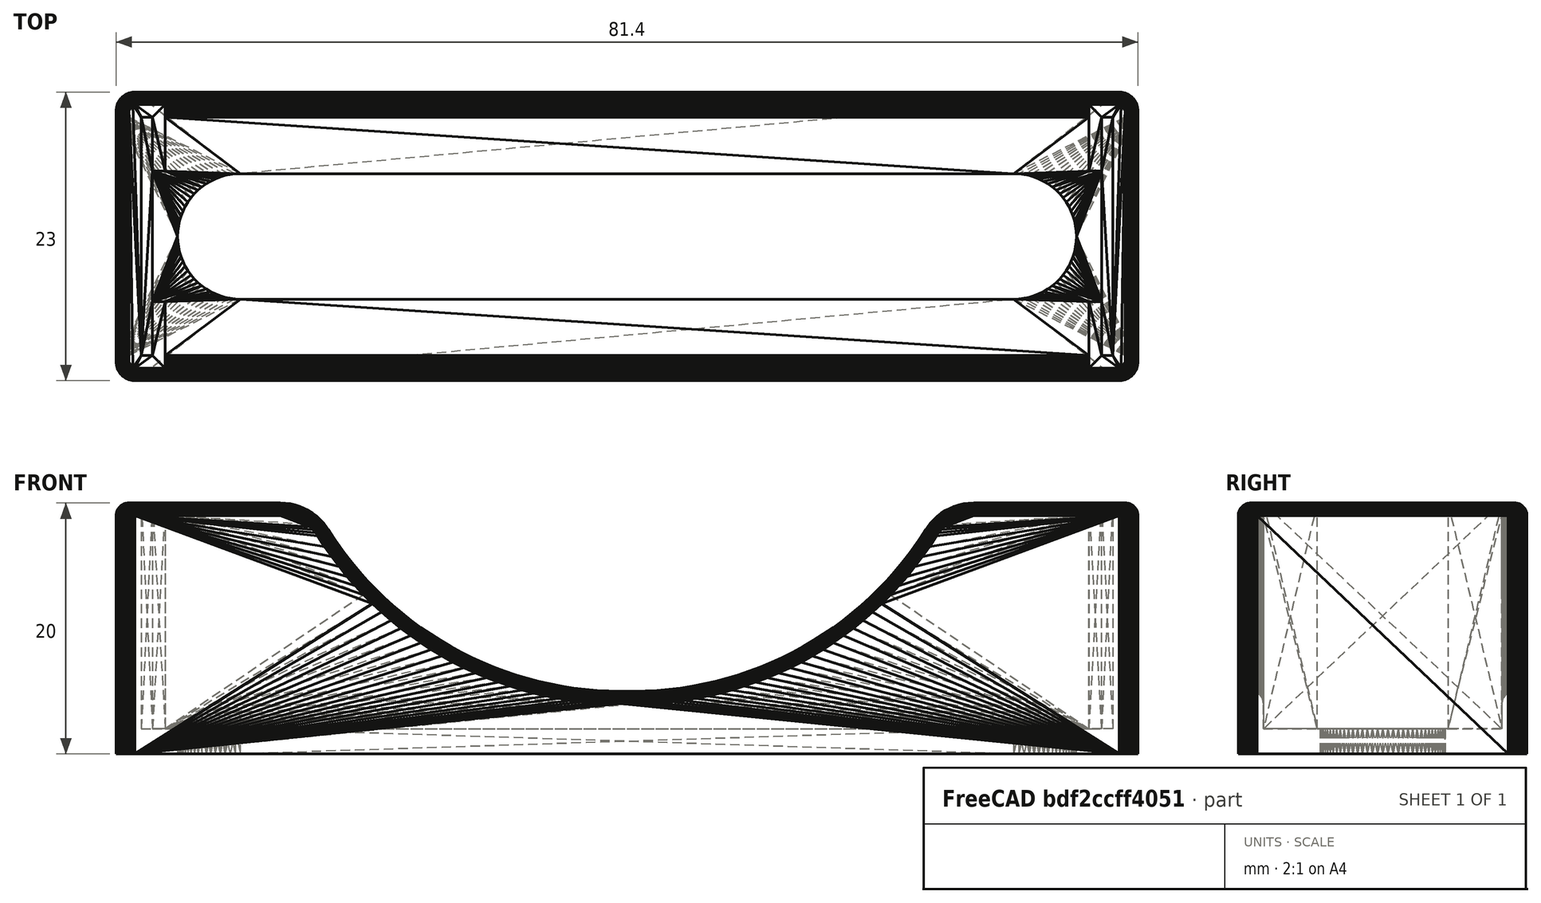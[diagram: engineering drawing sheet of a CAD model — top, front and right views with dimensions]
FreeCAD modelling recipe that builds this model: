
FCSTD DOCUMENT  (FreeCAD 0.21R33771 (Git))
Label: original battery holder measurements
License: All rights reserved
LicenseURL: https://en.wikipedia.org/wiki/All_rights_reserved
objects: App::MeasureDistance×10, Sketcher::SketchObject×1, PartDesign::Body×1, Mesh::Feature×1, Part::Feature×1
note: 3 computed .brp shape members not serialized (recipe doc carries the construction recipe); baked Part::Feature solids carry a one-line shape summary decoded from their .brp

FEATURE [App::MeasureDistance] Distance001  label="Distance: 73.58 mm"
  Distance = 73.5833
  P1 = (3.90567,2.00405,2)
  P2 = (77.489,2.00615,2)
FEATURE [Sketcher::SketchObject] Sketch
  FullyConstrained = false
  MapMode = 5
  Placement = pos=(0,0,0) rot=(0.57735,0.57735,0.57735;2.0944rad)
  Support = -> [YZ_Plane]
  sketch-geometry (4):
    g0: LineSegment StartX=0 StartY=0 StartZ=0 EndX=22.7593 EndY=0 EndZ=0
    g1: LineSegment StartX=22.7593 StartY=0 StartZ=0 EndX=22.7593 EndY=20 EndZ=0
    g2: LineSegment StartX=22.7593 StartY=20 StartZ=0 EndX=0 EndY=20 EndZ=0
    g3: LineSegment StartX=0 StartY=20 StartZ=0 EndX=0 EndY=0 EndZ=0
  constraints (9):
    c: Coincident(g0,g1)
    c: Coincident(g1,g2)
    c: Coincident(g2,g3)
    c: Coincident(g3,g0)
    c: Horizontal(g0)
    c: Horizontal(g2)
    c: Vertical(g1)
    c: Vertical(g3)
    c: Coincident(g0,g-1)
FEATURE [PartDesign::Body] Body
  Group = -> [Sketch]
  Origin = -> Origin
  Placement = pos=(0.869,0.145,0) rot=(0,0,1;0rad)
FEATURE [Mesh::Feature] __Batterie_2_0  label="1_Batterie_2.0"
FEATURE [App::MeasureDistance] Distance  label="Distance: 0.90 mm"
  Distance = 0.898536
  P1 = (2.90044,2.00754,20)
  P2 = (2.00334,2,19.9496)
FEATURE [App::MeasureDistance] Distance002  label="Distance: 17.89 mm"
  Distance = 17.8938
  P1 = (3.87948,6.3204,2)
  P2 = (3.8517,6.3,19.8937)
FEATURE [App::MeasureDistance] Distance003  label="Distance: 19.01 mm"
  Distance = 19.0145
  P1 = (2.01075,21.0145,20)
  P2 = (2.00009,2,19.9731)
FEATURE [App::MeasureDistance] Distance004  label="Distance: 0.99 mm"
  Distance = 0.989014
  P1 = (78.4982,16.7079,20)
  P2 = (77.5093,16.7208,20)
FEATURE [App::MeasureDistance] Distance005  label="Distance: 1.69 mm"
  Distance = 1.68771
  P1 = (75.242,0.54455,19.8874)
  P2 = (75.0612,1.99788,19.0486)
FEATURE [App::MeasureDistance] Distance006  label="Distance: 1.97 mm"
  Distance = 1.97069
  P1 = (79.4,10.4491,19.4513)
  P2 = (81.3611,10.5237,19.2721)
FEATURE [App::MeasureDistance] Distance007  label="Distance: 1.92 mm"
  Distance = 1.91553
  P1 = (41.4731,6.5,0.0176353)
  P2 = (41.467,6.5,1.93316)
FEATURE [Part::Feature] __Batterie_2_001
  shape: bbox 81.4 x 23 x 20 mm, 8812 faces, 0 solids (baked)
FEATURE [App::MeasureDistance] Distance008  label="Distance: 19.77 mm"
  Distance = 19.7693
  P1 = (0,21.5,0)
  P2 = (0.357212,21.5,19.766)
FEATURE [App::MeasureDistance] Distance009  label="Distance: 4.30 mm"
  Distance = 4.2995
  P1 = (2.92831,16.7,20)
  P2 = (2.92129,20.9995,20)
